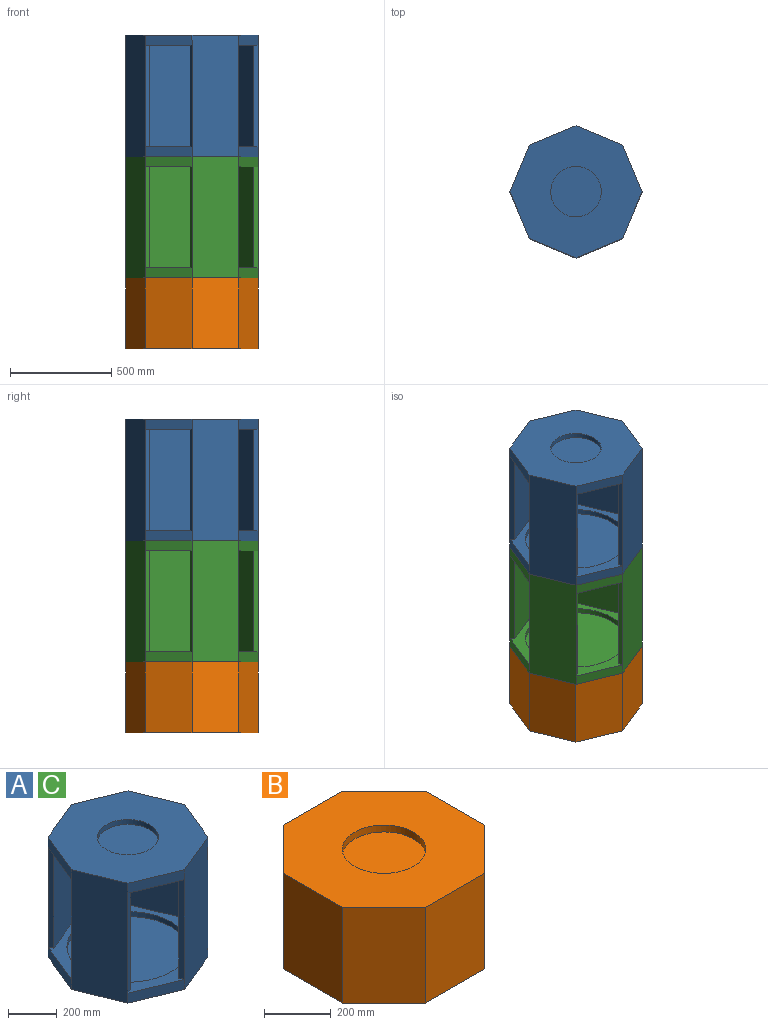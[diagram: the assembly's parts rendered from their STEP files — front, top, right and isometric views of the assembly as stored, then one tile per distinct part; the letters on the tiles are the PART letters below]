
ASSEMBLY  parts=3 mates=2
PART A: 34 faces, bbox 653.3x653.3x625 mm
  f0: plane 653.28x653.28mm, normal (0,0,1), area 80427.2mm2, adj f2,f4,f6,f8,f10,f11,f12,f13
  f1: plane 600x230.97mm, normal (0.38,-0.92,0), area 150000mm2, adj f2,f8,f9,f13,f14,f22,f25,f26
  f2: plane 230.97x95.67mm, normal (0.92,-0.38,0), area 12500mm2, adj f0,f1,f3,f9
  f3: plane 600x230.97mm, normal (0.92,0.38,0), area 150000mm2, adj f2,f4,f9,f16,f17,f22,f23,f26
  f4: plane 230.97x95.67mm, normal (0.38,0.92,0), area 12500mm2, adj f0,f3,f5,f9
  f5: plane 600x230.97mm, normal (-0.38,0.92,0), area 150000mm2, adj f4,f6,f9,f19,f20,f23,f24,f26
  f6: plane 230.97x95.67mm, normal (-0.92,0.38,0), area 12500mm2, adj f0,f5,f7,f9
  f7: plane 600x230.97mm, normal (-0.92,-0.38,0), area 150000mm2, adj f6,f8,f9,f10,f11,f24,f25,f26
  f8: plane 230.97x95.67mm, normal (-0.38,-0.92,0), area 12500mm2, adj f0,f1,f7,f9
  f9: plane 653.28x653.28mm, normal (0,0,-1), area 252689.3mm2, adj f1,f2,f3,f4,f5,f6,f7,f8
  f10: plane 500x23.1mm, normal (-0.38,0.92,0), area 12500mm2, adj f0,f7,f12,f27
  f11: plane 500x23.1mm, normal (0.38,-0.92,0), area 12500mm2, adj f0,f7,f12,f27
  f12: plane 500x230.97mm, normal (0.92,0.38,0), area 125000mm2, adj f0,f10,f11,f27
  f13: plane 500x23.1mm, normal (-0.92,-0.38,0), area 12500mm2, adj f0,f1,f15,f27
  f14: plane 500x23.1mm, normal (0.92,0.38,0), area 12500mm2, adj f0,f1,f15,f27
  f15: plane 500x230.97mm, normal (-0.38,0.92,0), area 125000mm2, adj f0,f13,f14,f27
  f16: plane 500x23.1mm, normal (0.38,-0.92,0), area 12500mm2, adj f0,f3,f18,f27
  f17: plane 500x23.1mm, normal (-0.38,0.92,0), area 12500mm2, adj f0,f3,f18,f27
  f18: plane 500x230.97mm, normal (-0.92,-0.38,0), area 125000mm2, adj f0,f16,f17,f27
  f19: plane 500x23.1mm, normal (0.92,0.38,0), area 12500mm2, adj f0,f5,f21,f27
  f20: plane 500x23.1mm, normal (-0.92,-0.38,0), area 12500mm2, adj f0,f5,f21,f27
  f21: plane 500x230.97mm, normal (0.38,-0.92,0), area 125000mm2, adj f0,f19,f20,f27
  f22: plane 230.97x95.67mm, normal (0.92,-0.38,0), area 12500mm2, adj f1,f3,f26,f27
  f23: plane 230.97x95.67mm, normal (0.38,0.92,0), area 12500mm2, adj f3,f5,f26,f27
  f24: plane 230.97x95.67mm, normal (-0.92,0.38,0), area 12500mm2, adj f5,f7,f26,f27
  f25: plane 230.97x95.67mm, normal (-0.38,-0.92,0), area 12500mm2, adj f1,f7,f26,f27
  f26: plane 653.28x653.28mm, normal (0,0,1), area 252689.3mm2, adj f1,f3,f5,f7,f22,f23,f24,f25
  f27: plane 653.28x653.28mm, normal (0,0,-1), area 276776.7mm2, adj f10,f11,f12,f13,f14,f15,f16,f17
  f28: cylinder r=250mm len=500mm, axis (0,0,1), area 39269.9mm2, adj f0,f29
  f29: plane 500x500mm, normal (0,0,1), area 196349.5mm2, adj f28
  f30: cylinder r=125mm len=250mm, axis (0,0,1), area 19635mm2, adj f9,f31
  f31: plane 250x250mm, normal (0,0,-1), area 49087.4mm2, adj f30
  f32: cylinder r=125mm len=250mm, axis (0,0,1), area 19635mm2, adj f26,f33
  f33: plane 250x250mm, normal (0,0,1), area 49087.4mm2, adj f32
PART B: 12 faces, bbox 603.6x603.6x350 mm
  f0: plane 350x176.78mm, normal (0.71,-0.71,0), area 87500mm2, adj f1,f7,f8,f9
  f1: plane 350x250mm, normal (1,0,0), area 87500mm2, adj f0,f2,f8,f9
  f2: plane 350x176.78mm, normal (0.71,0.71,0), area 87500mm2, adj f1,f3,f8,f9
  f3: plane 350x250mm, normal (0,1,0), area 87500mm2, adj f2,f4,f8,f9
  f4: plane 350x176.78mm, normal (-0.71,0.71,0), area 87500mm2, adj f3,f5,f8,f9
  f5: plane 350x250mm, normal (-1,0,0), area 87500mm2, adj f4,f6,f8,f9
  f6: plane 350x176.78mm, normal (-0.71,-0.71,0), area 87500mm2, adj f5,f7,f8,f9
  f7: plane 350x250mm, normal (0,-1,0), area 87500mm2, adj f0,f6,f8,f9
  f8: plane 603.55x603.55mm, normal (0,0,1), area 252689.3mm2, adj f0,f1,f2,f3,f4,f5,f6,f7
  f9: plane 603.55x603.55mm, normal (0,0,-1), area 301776.7mm2, adj f0,f1,f2,f3,f4,f5,f6,f7
  f10: cylinder r=125mm len=250mm, axis (0,0,1), area 19635mm2, adj f8,f11
  f11: plane 250x250mm, normal (0,0,1), area 49087.4mm2, adj f10
PART C: same geometry as A
PLACE A t=(-66.81,18.75,502.7)mm
PLACE B rot(axis=(0,0,-1),22.5deg) t=(-66.81,18.75,-447.3)mm
PLACE C t=(-66.81,18.75,-97.3)mm
MATE revolute B.f10 <-> C.f30  axis (0,0,1) through (-66.81,18.75,-122.3)mm
MATE fastened A.f30 <-> C.f32  axis (0,0,-1) through (-66.81,18.75,477.7)mm
